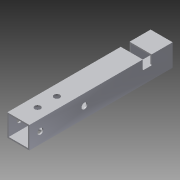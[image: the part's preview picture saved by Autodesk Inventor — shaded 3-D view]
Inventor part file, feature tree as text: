
AUTODESK INVENTOR PART (.ipt)
format: ipt  version: 2013 (Build 170138000, 138)  size: 113,152 bytes
history: native  units: in
note: dims shown in document units (in); Inventor stores cm internally (conversion verified against a paired STEP export)
features: reference x5, extrude x4, sketch x4
ambient origin geometry x8: Origin, YZ Plane, XZ Plane, XY Plane, X Axis, Y Axis, Z Axis, Center Point
bodies: Solid1 (feature_tree)
feature tree (13):
  extrude  "Extrusion1"  Depth=1.0in
  extrude  "Extrusion2"  Depth=6.5in TaperAngle=0.0deg
  extrude  "Extrusion3"  Depth=1.0in TaperAngle=0.0deg
  extrude  "Extrusion4"  [1 undecoded]
  sketch  "Sketch1"  dims[d0=1.0in d1=1.0in]
  sketch  "Sketch2"  dims[d2=0.0625in d3=6.5in d4=0.0in]
  reference  "Reference1"
  sketch  "Sketch3"  dims[d5=1.0in d6=0.0in d7=1.0in d8=0.0in]
  reference  "Reference2"
  reference  "Reference3"
  sketch  "Sketch4"  dims[d9=1.0in d10=0.0in]
  reference  "Reference4"
  reference  "Reference5"
note: 1 required parameter value undecoded (feature->parameter linkage not recoverable at this tier; creation-order binding heuristic only, values carry confidence <= 0.55)
